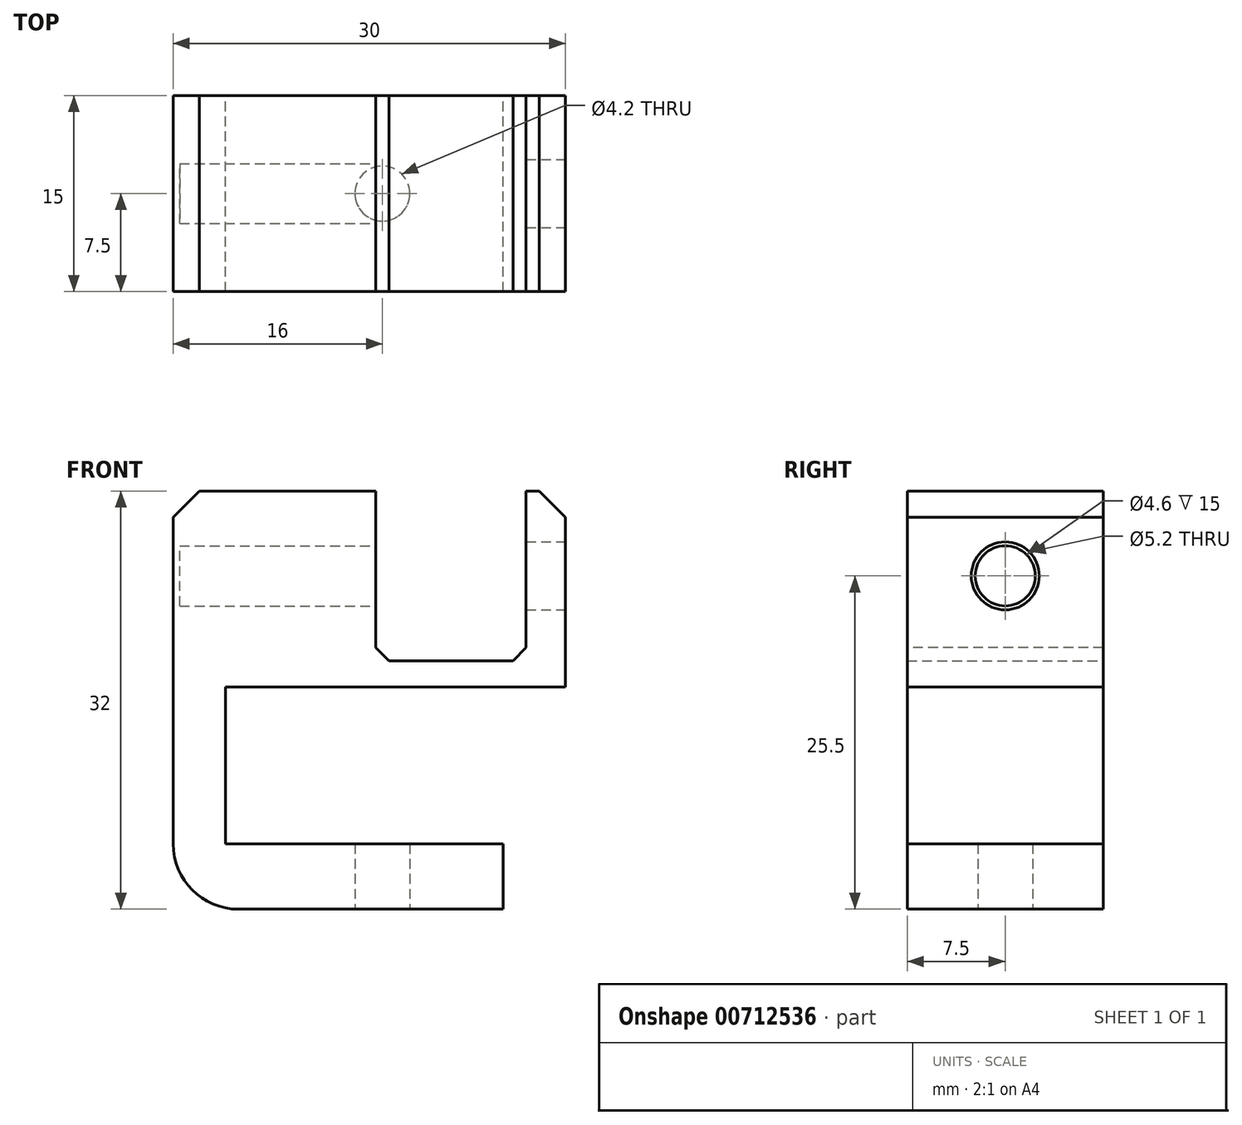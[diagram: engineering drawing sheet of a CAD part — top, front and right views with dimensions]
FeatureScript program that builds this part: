
annotation { "Feature Type Name" : "Feature", "Feature Type Description" : "" }
export const myFeature = defineFeature(function(context is Context, id is Id, definition is map)
    precondition{}
    {
        {
            var Q0;
            Q0=qCreatedBy(makeId("Front.planeOp"),FACE);
            var sketch = newSketch(context, id + "F0", { "sketchPlane" : qUnion([Q0])});
            skLineSegment(sketch, "E0", {"start": v(0, 5) * mm, "end": v(0, 32) * mm});
            skLineSegment(sketch, "E1", {"start": v(0, 32) * mm, "end": v(15.5, 32) * mm});
            skLineSegment(sketch, "E2", {"start": v(15.5, 32) * mm, "end": v(15.5, 19) * mm});
            skLineSegment(sketch, "E3", {"start": v(15.5, 19) * mm, "end": v(27, 19) * mm});
            skLineSegment(sketch, "E4", {"start": v(27, 19) * mm, "end": v(27, 32) * mm});
            skLineSegment(sketch, "E5", {"start": v(27, 32) * mm, "end": v(30, 32) * mm});
            skLineSegment(sketch, "E6", {"start": v(30, 32) * mm, "end": v(30, 17) * mm});
            skLineSegment(sketch, "E7", {"start": v(30, 17) * mm, "end": v(4, 17) * mm});
            skLineSegment(sketch, "E8", {"start": v(4, 17) * mm, "end": v(4, 5) * mm});
            skLineSegment(sketch, "E9", {"start": v(4, 5) * mm, "end": v(25.25, 5) * mm});
            skLineSegment(sketch, "E10", {"start": v(25.25, 5) * mm, "end": v(25.25, 0) * mm});
            skLineSegment(sketch, "E11", {"start": v(25.25, 0) * mm, "end": v(5, 0) * mm});
            skPoint(sketch, "E12.visualSharp", {"position": v(0, 0) * mm});
            skArc(sketch, "E12.filletArc", {"start": v(0, 5) * mm, "mid": v(1.46, 1.46) * mm, "end": v(5, 0) * mm});
            skSolve(sketch);
        }
        {
            var Q0;
            Q0=makeQuery(id+"F0.imprint","IMPRINT",FACE,{"disambiguationData":[TD([[makeQuery(id+"F0.imprint","IMPRINT",EDGE,{"derivedFrom":sQuery(id+"F0.wireOp",EDGE,"E0")}),-1.0]])]});
            extrude(context, id + "F1", {"entities" : qUnion([Q0]), "depth" : 15 * mm, "offsetDistance" : 25 * mm});
        }
        {
            var Q0;
            Q0=makeQuery(id+"F1.opExtrude","SWEPT_EDGE",EDGE,{"disambiguationData":[OSD([sQuery(id+"F0.wireOp",EDGE,"E0"),sQuery(id+"F0.wireOp",EDGE,"E1")])]});
            var Q1;
            Q1=makeQuery(id+"F1.opExtrude","SWEPT_EDGE",EDGE,{"disambiguationData":[OSD([sQuery(id+"F0.wireOp",EDGE,"E5"),sQuery(id+"F0.wireOp",EDGE,"E6")])]});
            chamfer(context, id + "F2", {"entities" : qUnion([Q0, Q1]), "width" : 2 * mm, "tangentPropagation" : true});
        }
        {
            var Q0;
            Q0=makeQuery(id+"F1.opExtrude","SWEPT_EDGE",EDGE,{"disambiguationData":[OSD([sQuery(id+"F0.wireOp",EDGE,"E2"),sQuery(id+"F0.wireOp",EDGE,"E3")])]});
            var Q1;
            Q1=makeQuery(id+"F1.opExtrude","SWEPT_EDGE",EDGE,{"disambiguationData":[OSD([sQuery(id+"F0.wireOp",EDGE,"E3"),sQuery(id+"F0.wireOp",EDGE,"E4")])]});
            chamfer(context, id + "F3", {"entities" : qUnion([Q0, Q1]), "width" : 1 * mm, "tangentPropagation" : true});
        }
        {
            var Q0;
            Q0=makeQuery(id+"F1.opExtrude","SWEPT_FACE",FACE,{"disambiguationData":[OSD([sQuery(id+"F0.wireOp",EDGE,"E11")])]});
            var sketch = newSketch(context, id + "F4", { "sketchPlane" : qUnion([Q0])});
            skCircle(sketch, "E13", {"center": v(16, 7.5) * mm, "radius": 2.1 * mm});
            skSolve(sketch);
        }
        {
            var Q0;
            Q0=makeQuery(id+"F4.imprint","IMPRINT",FACE,{"disambiguationData":[TD([[makeQuery(id+"F4.imprint","IMPRINT",EDGE,{"derivedFrom":sQuery(id+"F4.wireOp",EDGE,"E13")}),1.0]])]});
            extrude(context, id + "F5", {"entities" : qUnion([Q0]), "operationType" : NewBodyOperationType.REMOVE, "endBound" : BoundingType.UP_TO_NEXT, "oppositeDirection" : true, "depth" : 25 * mm, "offsetDistance" : 25 * mm});
        }
        {
            var Q0;
            Q0=makeQuery(id+"F1.opExtrude","SWEPT_FACE",FACE,{"disambiguationData":[OSD([sQuery(id+"F0.wireOp",EDGE,"E6")])]});
            var sketch = newSketch(context, id + "F6", { "sketchPlane" : qUnion([Q0])});
            skCircle(sketch, "E14", {"center": v(-7.5, 25.5) * mm, "radius": 2.3 * mm});
            skSolve(sketch);
        }
        {
            var Q0;
            Q0=makeQuery(id+"F6.imprint","IMPRINT",FACE,{"disambiguationData":[TD([[makeQuery(id+"F6.imprint","IMPRINT",EDGE,{"derivedFrom":sQuery(id+"F6.wireOp",EDGE,"E14")}),1.0]])]});
            extrude(context, id + "F7", {"entities" : qUnion([Q0]), "operationType" : NewBodyOperationType.REMOVE, "oppositeDirection" : true, "depth" : 29.5 * mm, "offsetDistance" : 25 * mm});
        }
        {
            var Q0;
            Q0=makeQuery(id+"F1.opExtrude","SWEPT_FACE",FACE,{"disambiguationData":[OSD([sQuery(id+"F0.wireOp",EDGE,"E6")])]});
            var sketch = newSketch(context, id + "F8", { "sketchPlane" : qUnion([Q0])});
            skCircle(sketch, "E15", {"center": v(-7.5, 25.5) * mm, "radius": 2.6 * mm});
            skSolve(sketch);
        }
        {
            var Q0;
            Q0=makeQuery(id+"F8.imprint","IMPRINT",FACE,{"disambiguationData":[TD([[makeQuery(id+"F8.imprint","IMPRINT",EDGE,{"derivedFrom":sQuery(id+"F8.wireOp",EDGE,"E15")}),1.0]])]});
            extrude(context, id + "F9", {"entities" : qUnion([Q0]), "operationType" : NewBodyOperationType.REMOVE, "endBound" : BoundingType.UP_TO_NEXT, "oppositeDirection" : true, "depth" : 25 * mm, "offsetDistance" : 25 * mm});
        }
    });
